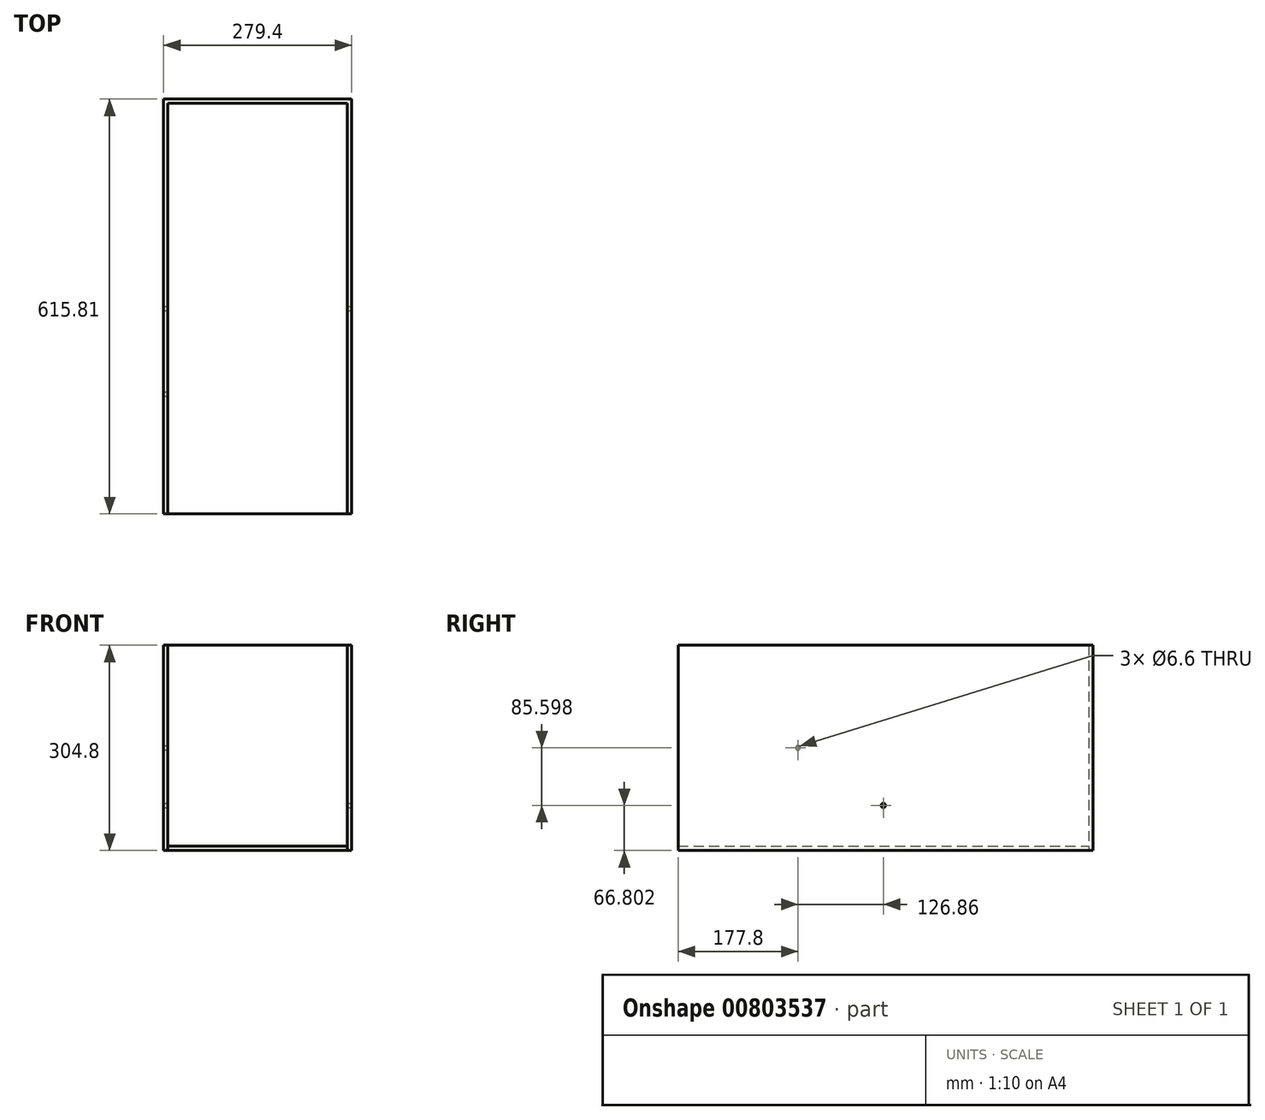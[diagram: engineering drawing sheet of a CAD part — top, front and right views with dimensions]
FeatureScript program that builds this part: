
annotation { "Feature Type Name" : "Feature", "Feature Type Description" : "" }
export const myFeature = defineFeature(function(context is Context, id is Id, definition is map)
    precondition{}
    {
        {
            var Q0;
            Q0=qCreatedBy(makeId("Top.planeOp"),FACE);
            var sketch = newSketch(context, id + "F0", { "sketchPlane" : qUnion([Q0])});
            skLineSegment(sketch, "E0.top", {"start": v(133.35, 304.8) * mm, "end": v(-133.35, 304.8) * mm});
            skLineSegment(sketch, "E0.left", {"start": v(133.35, -304.8) * mm, "end": v(133.35, 304.8) * mm});
            skLineSegment(sketch, "E0.right", {"start": v(-133.35, -304.8) * mm, "end": v(-133.35, 304.8) * mm});
            skPoint(sketch, "E0.middle", {"position": v(0, 0) * mm});
            skLineSegment(sketch, "E1.0", {"start": v(139.7, -304.66) * mm, "end": v(139.7, 311.15) * mm});
            skLineSegment(sketch, "E1.1", {"start": v(139.7, -304.66) * mm, "end": v(-139.7, -304.66) * mm});
            skLineSegment(sketch, "E1.2", {"start": v(-139.7, -304.66) * mm, "end": v(-139.7, 311.15) * mm});
            skLineSegment(sketch, "E1.3", {"start": v(139.7, 311.15) * mm, "end": v(-139.7, 311.15) * mm});
            skSolve(sketch);
        }
        {
            var Q0;
            {var subQ0=sQuery(id+"F0.wireOp",EDGE,"E0.top");Q0=makeQuery(id+"F0.imprint","IMPRINT",FACE,{"disambiguationData":[TD([[makeQuery(id+"F0.imprint","IMPRINT",EDGE,{"derivedFrom":subQ0}),1.0]])]});}
            extrude(context, id + "F1", {"entities" : qUnion([Q0]), "depth" : 6.35 * mm, "offsetDistance" : 25.4 * mm});
        }
        {
            var Q0;
            {var subQ2=sQuery(id+"F0.wireOp",EDGE,"E0.top");Q0=makeQuery(id+"F0.imprint","IMPRINT",FACE,{"disambiguationData":[TD([[makeQuery(id+"F0.imprint","IMPRINT",EDGE,{"derivedFrom":subQ2}),-1.0]])]});}
            extrude(context, id + "F2", {"entities" : qUnion([Q0]), "depth" : 304.8 * mm, "offsetDistance" : 25.4 * mm});
        }
        {
            var Q0;
            Q0=makeQuery(id+"F2.opExtrude","SWEPT_FACE",FACE,{"disambiguationData":[OSD([sQuery(id+"F0.wireOp",EDGE,"E1.0")])]});
            var sketch = newSketch(context, id + "F3", { "sketchPlane" : qUnion([Q0])});
            skCircle(sketch, "E2", {"center": v(0, 66.8) * mm, "radius": 3.3 * mm});
            skSolve(sketch);
        }
        {
            var Q0;
            Q0=makeQuery(id+"F3.imprint","IMPRINT",FACE,{"disambiguationData":[TD([[makeQuery(id+"F3.imprint","IMPRINT",EDGE,{"derivedFrom":sQuery(id+"F3.wireOp",EDGE,"E2")}),1.0]])]});
            extrude(context, id + "F4", {"entities" : qUnion([Q0]), "operationType" : NewBodyOperationType.REMOVE, "endBound" : BoundingType.THROUGH_ALL, "oppositeDirection" : true, "depth" : 25.4 * mm, "offsetDistance" : 25.4 * mm});
        }
        {
            var Q0;
            Q0=makeQuery(id+"F2.opExtrude","SWEPT_FACE",FACE,{"disambiguationData":[OSD([sQuery(id+"F0.wireOp",EDGE,"E0.right")])]});
            var sketch = newSketch(context, id + "F5", { "sketchPlane" : qUnion([Q0])});
            skCircle(sketch, "E3", {"center": v(-126.86, 152.4) * mm, "radius": 3.3 * mm});
            skSolve(sketch);
        }
        {
            var Q0;
            Q0 = qSketchRegion(id + "F5", true);
            extrude(context, id + "F6", {"entities" : qUnion([Q0]), "operationType" : NewBodyOperationType.REMOVE, "oppositeDirection" : true, "depth" : 25.4 * mm, "offsetDistance" : 25.4 * mm});
        }
    });
